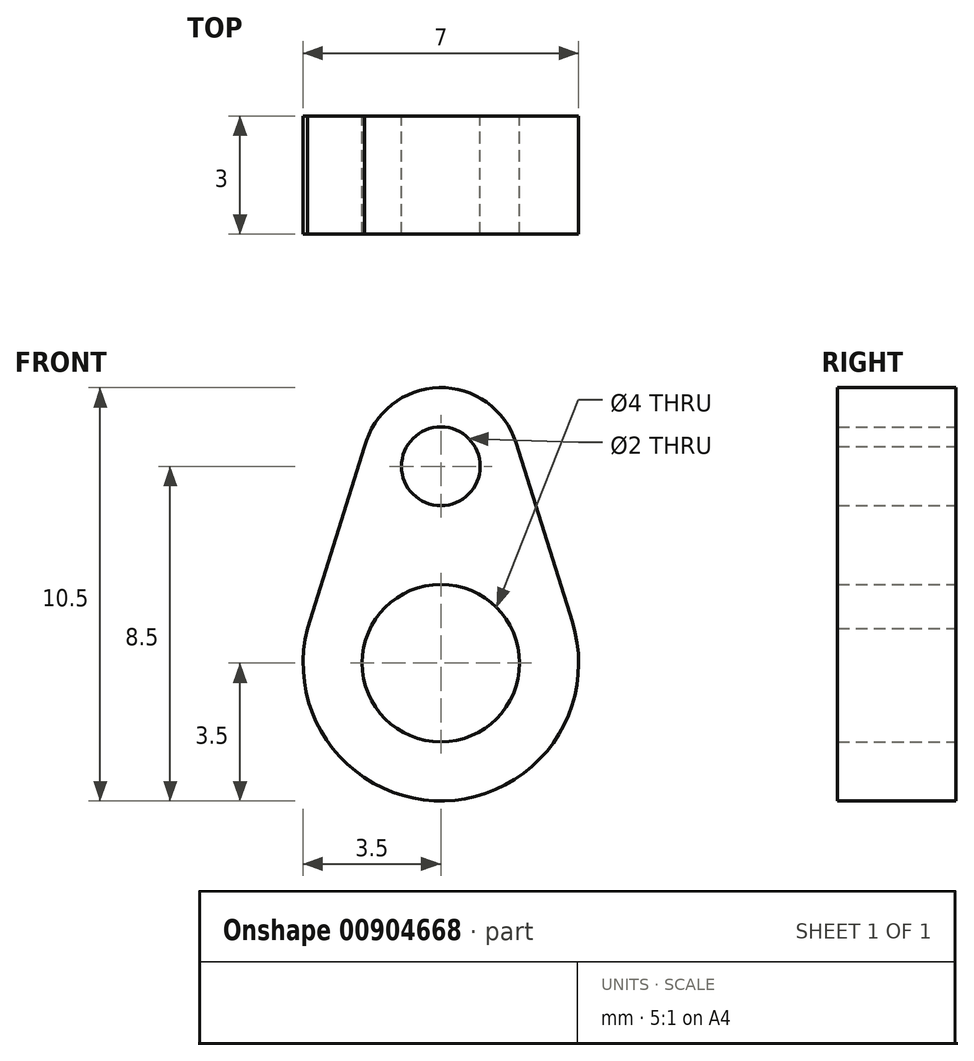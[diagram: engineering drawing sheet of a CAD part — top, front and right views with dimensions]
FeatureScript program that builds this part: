
annotation { "Feature Type Name" : "Feature", "Feature Type Description" : "" }
export const myFeature = defineFeature(function(context is Context, id is Id, definition is map)
    precondition{}
    {
        {
            var Q0;
            Q0=qCreatedBy(makeId("Front.planeOp"),FACE);
            var sketch = newSketch(context, id + "F0", { "sketchPlane" : qUnion([Q0])});
            skArc(sketch, "E0", {"start": v(1.9, 5.6) * mm, "mid": v(-0.3, 6.98) * mm, "end": v(-2, 5) * mm});
            skCircle(sketch, "E1", {"center": v(0, 0) * mm, "radius": 2 * mm});
            skLineSegment(sketch, "E2", {"start": v(1.9, 5.6) * mm, "end": v(3.34, 1.05) * mm});
            skArc(sketch, "E3", {"start": v(-3.39, 0.87) * mm, "mid": v(0.1, -3.5) * mm, "end": v(3.34, 1.05) * mm});
            skLineSegment(sketch, "E4.MirrorCS", {"start": v(-1.94, 5.5) * mm, "end": v(-3.39, 0.87) * mm});
            skPoint(sketch, "E5.orphan", {"position": v(-1.4, 7.24) * mm});
            skPoint(sketch, "E6.orphan", {"position": v(1.08, 8.22) * mm});
            skPoint(sketch, "E7.orphan", {"position": v(4.42, -2.39) * mm});
            skPoint(sketch, "E8.orphan", {"position": v(-4.72, -3.37) * mm});
            skCircle(sketch, "E9", {"center": v(0, 5) * mm, "radius": 1 * mm});
            skPoint(sketch, "E10.orphan", {"position": v(2, 5) * mm});
            skSolve(sketch);
        }
        {
            var Q0;
            Q0=makeQuery(id+"F0.imprint","IMPRINT",FACE,{"disambiguationData":[TD([[makeQuery(id+"F0.imprint","IMPRINT",EDGE,{"derivedFrom":sQuery(id+"F0.wireOp",EDGE,"E1")}),-1.0]])]});
            extrude(context, id + "F1", {"entities" : qUnion([Q0]), "depth" : 3 * mm, "offsetDistance" : 25 * mm});
        }
    });
